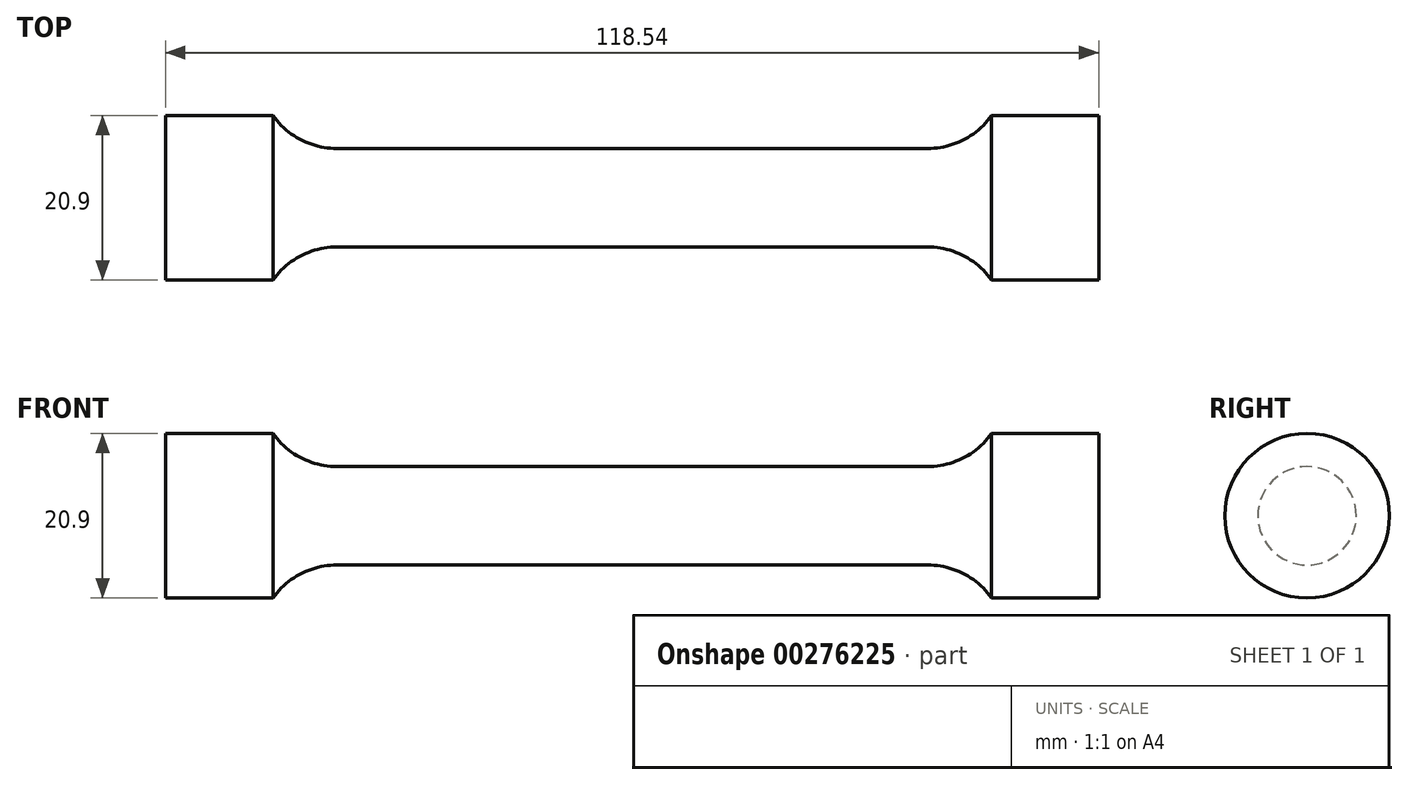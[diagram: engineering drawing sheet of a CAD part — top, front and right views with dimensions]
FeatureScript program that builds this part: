
annotation { "Feature Type Name" : "Feature", "Feature Type Description" : "" }
export const myFeature = defineFeature(function(context is Context, id is Id, definition is map)
    precondition{}
    {
        {
            var Q0;
            Q0=qCreatedBy(makeId("Front.planeOp"),FACE);
            var sketch = newSketch(context, id + "F0", { "sketchPlane" : qUnion([Q0])});
            skLineSegment(sketch, "E0", {"start": v(0, 6.25) * mm, "end": v(37.5, 6.25) * mm});
            skArc(sketch, "E1", {"start": v(37.5, 6.25) * mm, "mid": v(42.08, 7.36) * mm, "end": v(45.65, 10.45) * mm});
            skLineSegment(sketch, "E2", {"start": v(45.65, 10.45) * mm, "end": v(59.27, 10.45) * mm});
            skLineSegment(sketch, "E3", {"start": v(59.27, 10.45) * mm, "end": v(59.27, 0) * mm});
            skLineSegment(sketch, "E4", {"start": v(59.27, 0) * mm, "end": v(0, 0) * mm});
            skLineSegment(sketch, "E5.MirrorCS", {"start": v(0, 6.25) * mm, "end": v(-37.5, 6.25) * mm});
            skLineSegment(sketch, "E6.MirrorCS", {"start": v(-59.27, 0) * mm, "end": v(0, 0) * mm});
            skLineSegment(sketch, "E7.MirrorCS", {"start": v(-45.65, 10.45) * mm, "end": v(-59.27, 10.45) * mm});
            skLineSegment(sketch, "E8.MirrorCS", {"start": v(-59.27, 10.45) * mm, "end": v(-59.27, 0) * mm});
            skArc(sketch, "E9.MirrorCS", {"start": v(-37.5, 6.25) * mm, "mid": v(-42.08, 7.36) * mm, "end": v(-45.65, 10.45) * mm});
            skSolve(sketch);
        }
        {
            var Q0;
            Q0=makeQuery(id+"F0.imprint","IMPRINT",FACE,{"disambiguationData":[TD([[makeQuery(id+"F0.imprint","IMPRINT",EDGE,{"derivedFrom":sQuery(id+"F0.wireOp",EDGE,"E0")}),-1.0]])]});
            var Q1;
            Q1=sQuery(id+"F0.wireOp",EDGE,"E6.MirrorCS");
            revolve(context, id + "F1", {"entities" : qUnion([Q0]), "axis" : qUnion([Q1]), "revolveType" : RevolveType.FULL});
        }
    });
